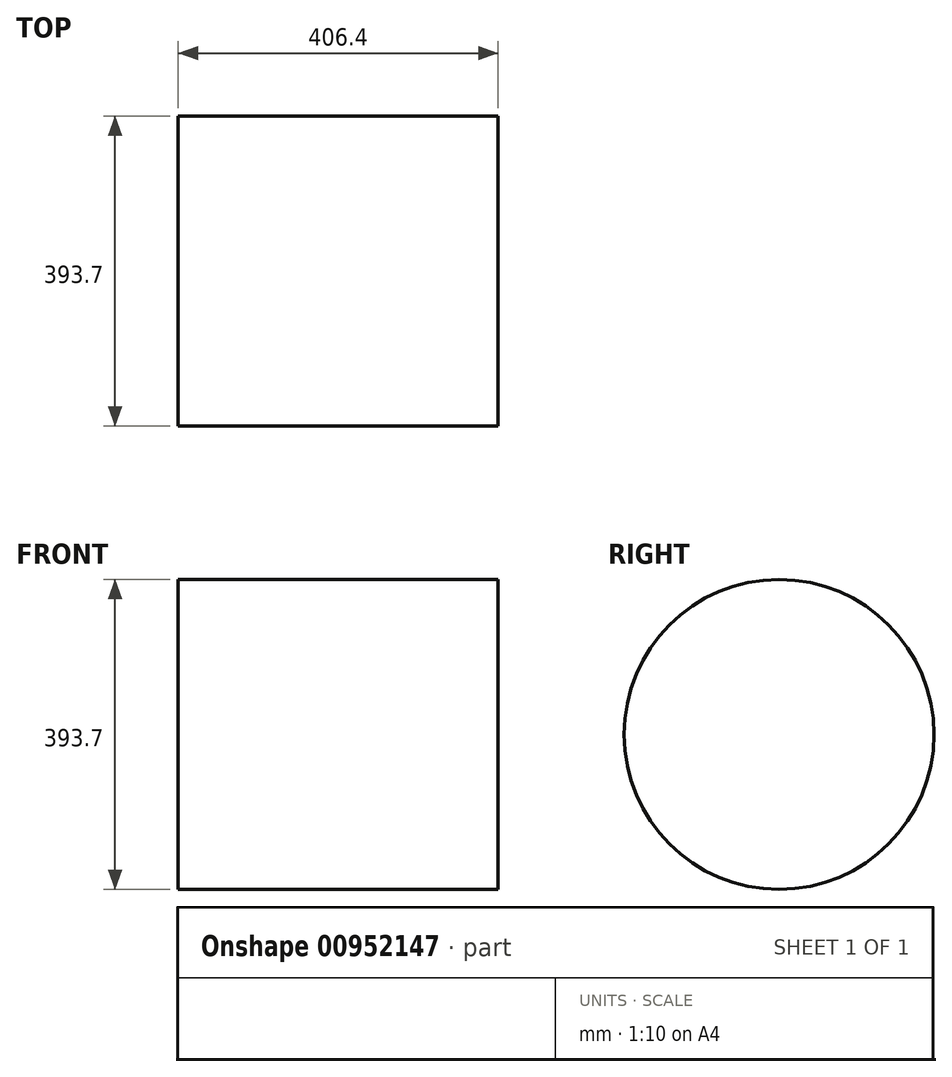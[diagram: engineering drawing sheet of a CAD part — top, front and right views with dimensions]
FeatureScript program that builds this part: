
annotation { "Feature Type Name" : "Feature", "Feature Type Description" : "" }
export const myFeature = defineFeature(function(context is Context, id is Id, definition is map)
    precondition{}
    {
        {
            var Q0;
            Q0=qCreatedBy(makeId("Right.planeOp"),FACE);
            var sketch = newSketch(context, id + "F0", { "sketchPlane" : qUnion([Q0])});
            skCircle(sketch, "E0", {"center": v(0, 0) * mm, "radius": 196.85 * mm});
            skSolve(sketch);
        }
        {
            var Q0;
            Q0=makeQuery(id+"F0.imprint","IMPRINT",FACE,{"disambiguationData":[TD([[makeQuery(id+"F0.imprint","IMPRINT",EDGE,{"derivedFrom":sQuery(id+"F0.wireOp",EDGE,"E0")}),1.0]])]});
            extrude(context, id + "F1", {"entities" : qUnion([Q0]), "depth" : 406.4 * mm, "offsetDistance" : 25.4 * mm});
        }
    });
